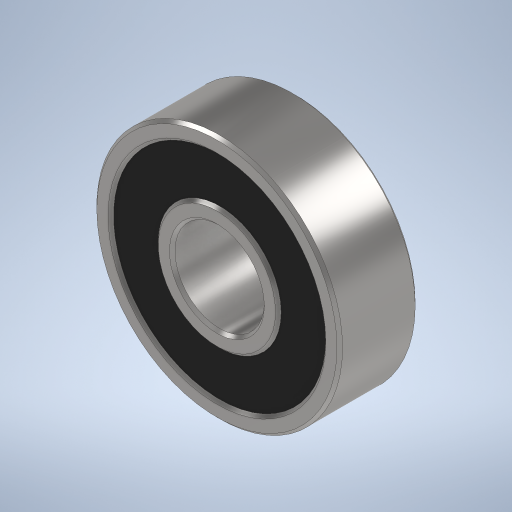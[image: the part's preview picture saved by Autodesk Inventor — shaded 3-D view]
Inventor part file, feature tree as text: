
AUTODESK INVENTOR PART (.ipt)
format: ipt  version: 2024 (Build 280153000, 153)  size: 292,864 bytes
history: native  units: mm
features: extrude x2, sketch x1, chamfer x1
ambient origin geometry x8: Origin, YZ Plane, XZ Plane, XY Plane, X Axis, Y Axis, Z Axis, Center Point
bodies: Solid1 (feature_tree)
feature tree (4):
  sketch  "Sketch1"  dims[d0=22.0mm d1=8.0mm d2=1.5mm d3=1.5mm d4=7.0mm d5=0.0mm d6=6.5mm d7=0.0mm d8=0.25mm d9=2.0mm d10=45.0deg]
  extrude  "Extrusion1"  Depth=0.25mm
  extrude  "Extrusion2"  Depth=0.25mm
  chamfer  "Chamfer1"  Distance=1.5mm
